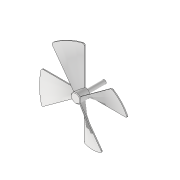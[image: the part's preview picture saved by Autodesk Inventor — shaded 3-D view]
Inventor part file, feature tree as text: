
AUTODESK INVENTOR PART (.ipt)
format: ipt  version: 2020 (Build 240168000, 168)  size: 143,360 bytes
history: native  units: mm
features: sketch x3, extrude x2, other x1, fillet x1, pattern_circular x1, chamfer x1
ambient origin geometry x8: Origin, YZ Plane, XZ Plane, XY Plane, X Axis, Y Axis, Z Axis, Center Point
bodies: Volumenkörper1 (feature_tree)
feature tree (9):
  extrude  "Extrusion1"  Depth=50.0mm TaperAngle=0.0deg
  extrude  "Extrusion2"  Depth=200.0mm TaperAngle=0.0deg
  other  "Spirale1"
  fillet  "Rundung1"  Radius=200.0mm
  pattern_circular  "Runde Anordnung1"  Count=5  [1 undecoded]
  chamfer  "Fase1"  [1 undecoded]
  sketch  "Skizze1"  dims[d0=50.0mm d1=50.0mm d2=0.0mm]
  sketch  "Skizze2"  dims[d3=20.0mm d4=150.0mm d5=0.0mm d6=200.0mm]
  sketch  "Skizze3"  dims[d7=5.0mm d8=50.0mm d10=400.0mm d11=10.0mm d12=1.0mm d13=0.0mm d14=90.0deg d15=90.0deg d16=0.0mm d17=0.0mm d18=0.0mm d19=8.0mm d20=40.0mm d21=360.0deg d23=3.0mm d24=2.0mm d25=45.0deg]
note: 2 required parameter values undecoded (feature->parameter linkage not recoverable at this tier; creation-order binding heuristic only, values carry confidence <= 0.55)
